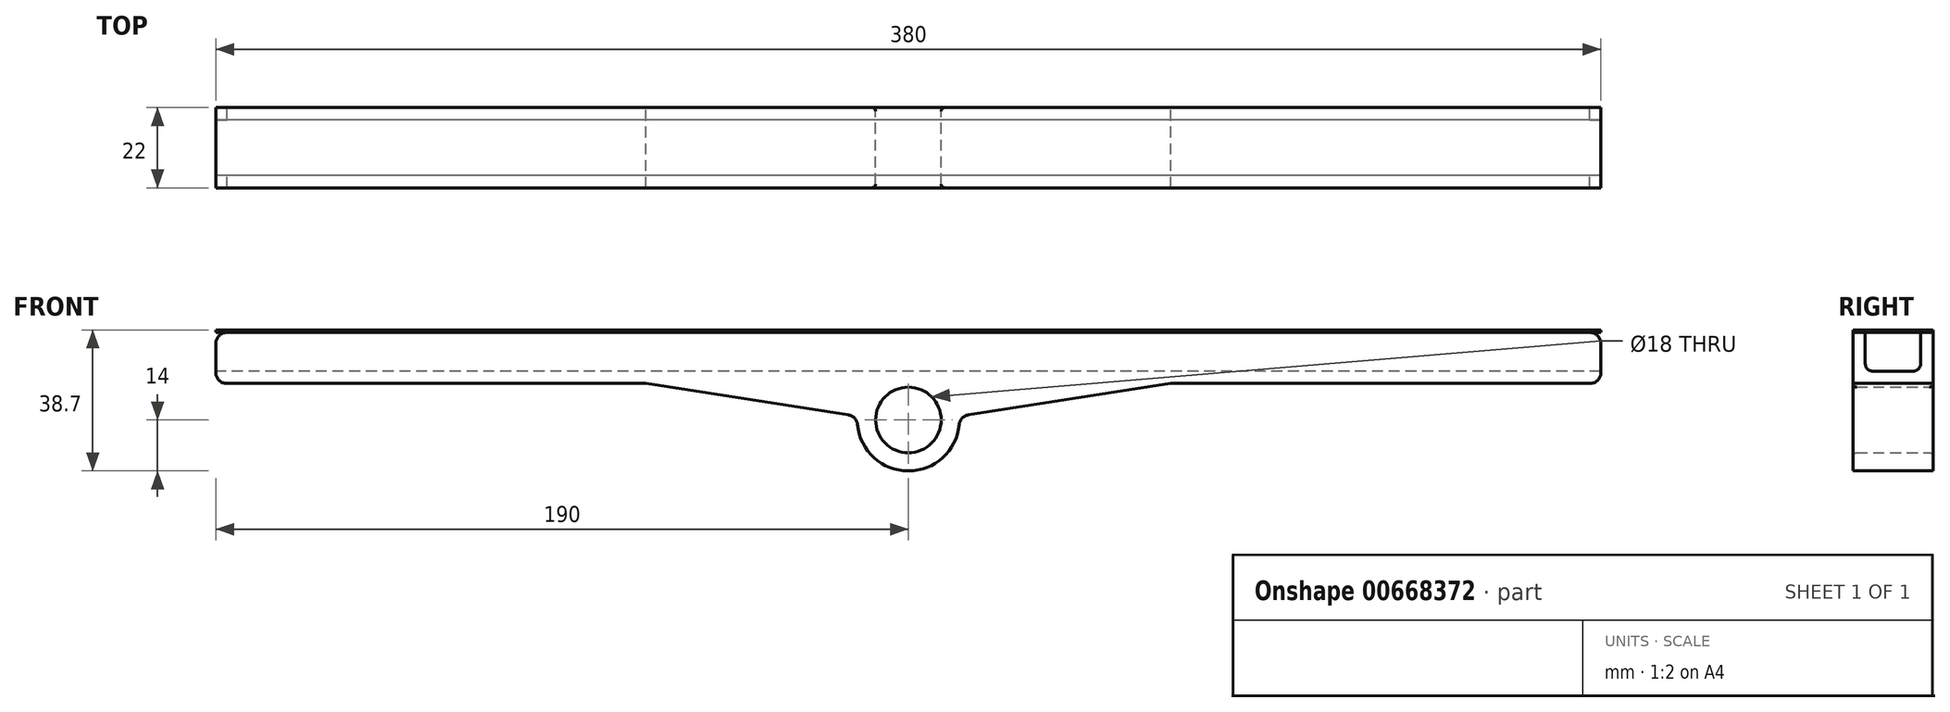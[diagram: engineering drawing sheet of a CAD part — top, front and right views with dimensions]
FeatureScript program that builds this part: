
annotation { "Feature Type Name" : "Feature", "Feature Type Description" : "" }
export const myFeature = defineFeature(function(context is Context, id is Id, definition is map)
    precondition{}
    {
        {
            assignVariable(context, id + "F0", {"name" : "TrayThickness", "anyValue" : 22});
        }
        {
            var Q0;
            Q0=qCreatedBy(makeId("Front.planeOp"),FACE);
            var sketch = newSketch(context, id + "F1", { "sketchPlane" : qUnion([Q0])});
            skLineSegment(sketch, "E0", {"start": v(-190, 159.54) * mm, "end": v(-190, -158.49) * mm, "construction": true});
            skLineSegment(sketch, "E1", {"start": v(190, 159.54) * mm, "end": v(190, -158.49) * mm, "construction": true});
            skLineSegment(sketch, "E2", {"start": v(-190, 14) * mm, "end": v(190, 14) * mm});
            skLineSegment(sketch, "E3", {"start": v(190, 14) * mm, "end": v(190, 0) * mm});
            skLineSegment(sketch, "E4", {"start": v(190, 0) * mm, "end": v(-190, 0) * mm});
            skLineSegment(sketch, "E5", {"start": v(-190, 0) * mm, "end": v(-190, 14) * mm});
            skSolve(sketch);
        }
        {
            var Q0;
            Q0=makeQuery(id+"F1.imprint","IMPRINT",FACE,{"disambiguationData":[TD([[makeQuery(id+"F1.imprint","IMPRINT",EDGE,{"derivedFrom":sQuery(id+"F1.wireOp",EDGE,"E2")}),-1.0]])]});
            extrude(context, id + "F2", {"entities" : qUnion([Q0]), "endBound" : BoundingType.SYMMETRIC, "depth" : (getVariable(context, 'TrayThickness')) * mm, "offsetDistance" : 25 * mm});
        }
        {
            var Q0;
            Q0=makeQuery(id+"F2.opExtrude","SWEPT_FACE",FACE,{"disambiguationData":[OSD([sQuery(id+"F1.wireOp",EDGE,"E5")])]});
            var sketch = newSketch(context, id + "F3", { "sketchPlane" : qUnion([Q0])});
            skLineSegment(sketch, "E6", {"start": v(-7.6, 14) * mm, "end": v(-7.6, 5.4) * mm});
            skLineSegment(sketch, "E7", {"start": v(-5.6, 3.4) * mm, "end": v(5.6, 3.4) * mm});
            skLineSegment(sketch, "E8", {"start": v(7.6, 5.4) * mm, "end": v(7.6, 14) * mm});
            skPoint(sketch, "E9.visualSharp", {"position": v(-7.6, 3.4) * mm});
            skArc(sketch, "E9.filletArc", {"start": v(-7.6, 5.4) * mm, "mid": v(-7.01, 3.99) * mm, "end": v(-5.6, 3.4) * mm});
            skPoint(sketch, "E10.visualSharp", {"position": v(7.6, 3.4) * mm});
            skArc(sketch, "E10.filletArc", {"start": v(5.6, 3.4) * mm, "mid": v(7.01, 3.99) * mm, "end": v(7.6, 5.4) * mm});
            skSolve(sketch);
        }
        {
            var Q0;
            {var subQ1=sQuery(id+"F3.wireOp",EDGE,"E6");Q0=makeQuery(id+"F3.imprint","IMPRINT",FACE,{"disambiguationData":[TD([[makeQuery(id+"F3.imprint","IMPRINT",EDGE,{"derivedFrom":subQ1}),1.0]])]});}
            extrude(context, id + "F4", {"entities" : qUnion([Q0]), "operationType" : NewBodyOperationType.REMOVE, "endBound" : BoundingType.THROUGH_ALL, "oppositeDirection" : true, "depth" : 25 * mm, "offsetDistance" : 25 * mm});
        }
        {
            var Q0;
            Q0=makeQuery(id+"F2.opExtrude","CAP_FACE",FACE,{"disambiguationData":[OSD([sQuery(id+"F1.wireOp",EDGE,"E2"),sQuery(id+"F1.wireOp",EDGE,"E3"),sQuery(id+"F1.wireOp",EDGE,"E4"),sQuery(id+"F1.wireOp",EDGE,"E5")])],"isStart":true});
            var sketch = newSketch(context, id + "F5", { "sketchPlane" : qUnion([Q0])});
            skLineSegment(sketch, "E11", {"start": v(-72, 0) * mm, "end": v(-13.96, -9) * mm});
            skCircle(sketch, "E12", {"center": v(0, -10) * mm, "radius": 9 * mm});
            skCircle(sketch, "E13", {"center": v(0, -10) * mm, "radius": 14 * mm});
            skLineSegment(sketch, "E14", {"start": v(13.96, -9) * mm, "end": v(72, 0) * mm});
            skSolve(sketch);
        }
        {
            var Q0;
            {var subQ0=sQuery(id+"F5.wireOp",EDGE,"E11");Q0=makeQuery(id+"F5.imprint","IMPRINT",FACE,{"disambiguationData":[TD([[makeQuery(id+"F5.imprint","IMPRINT",EDGE,{"derivedFrom":subQ0}),1.0]])]});}
            var Q1;
            Q1=makeQuery(id+"F5.imprint","IMPRINT",FACE,{"disambiguationData":[TD([[makeQuery(id+"F5.imprint","IMPRINT",EDGE,{"derivedFrom":sQuery(id+"F5.wireOp",EDGE,"E12")}),-1.0]])]});
            var Q2;
            {var subQ0=sQuery(id+"F5.wireOp",EDGE,"E14");Q2=makeQuery(id+"F5.imprint","IMPRINT",FACE,{"disambiguationData":[TD([[makeQuery(id+"F5.imprint","IMPRINT",EDGE,{"derivedFrom":subQ0}),1.0]])]});}
            var Q3;
            Q3=makeQuery(id+"F2.opExtrude","CAP_FACE",FACE,{"disambiguationData":[OSD([sQuery(id+"F1.wireOp",EDGE,"E2"),sQuery(id+"F1.wireOp",EDGE,"E3"),sQuery(id+"F1.wireOp",EDGE,"E4"),sQuery(id+"F1.wireOp",EDGE,"E5")])],"isStart":false});
            extrude(context, id + "F6", {"entities" : qUnion([Q0, Q1, Q2]), "operationType" : NewBodyOperationType.ADD, "endBound" : BoundingType.UP_TO_SURFACE, "oppositeDirection" : true, "depth" : 25 * mm, "endBoundEntityFace" : qUnion([Q3]), "offsetDistance" : 25 * mm});
        }
        {
            var Q0;
            {var subQ2=sQuery(id+"F1.wireOp",EDGE,"E2");Q0=makeQuery(id+"F4.boolean.opBoolean","SPLIT",FACE,{"disambiguationData":[TD([makeQuery(id+"F4.opExtrude","SWEPT_FACE",FACE,{"disambiguationData":[OSD([sQuery(id+"F3.wireOp",EDGE,"E8")])]})])],"derivedFrom":makeQuery(id+"F2.opExtrude","SWEPT_FACE",FACE,{"disambiguationData":[OSD([subQ2])]})});}
            var sketch = newSketch(context, id + "F7", { "sketchPlane" : qUnion([Q0])});
            skLineSegment(sketch, "E15.bottom", {"start": v(-190, 11) * mm, "end": v(190, 11) * mm});
            skLineSegment(sketch, "E15.top", {"start": v(-190, -11) * mm, "end": v(190, -11) * mm});
            skLineSegment(sketch, "E15.left", {"start": v(-190, 11) * mm, "end": v(-190, -11) * mm});
            skLineSegment(sketch, "E15.right", {"start": v(190, 11) * mm, "end": v(190, -11) * mm});
            skSolve(sketch);
        }
        {
            var Q0;
            {var subQ0=sQuery(id+"F1.wireOp",EDGE,"E2");var subQ1=sQuery(id+"F1.wireOp",EDGE,"E3");Q0=makeQuery(id+"F4.boolean.opBoolean","SPLIT",EDGE,{"disambiguationData":[TD([makeQuery(id+"F4.opExtrude","SWEPT_FACE",FACE,{"disambiguationData":[OSD([sQuery(id+"F3.wireOp",EDGE,"E8")])]})])],"derivedFrom":makeQuery(id+"F2.opExtrude","SWEPT_EDGE",EDGE,{"disambiguationData":[OSD([subQ0,subQ1])]})});}
            var Q1;
            {var subQ0=sQuery(id+"F1.wireOp",EDGE,"E2");var subQ1=sQuery(id+"F1.wireOp",EDGE,"E3");Q1=makeQuery(id+"F4.boolean.opBoolean","SPLIT",EDGE,{"disambiguationData":[TD([makeQuery(id+"F4.opExtrude","SWEPT_FACE",FACE,{"disambiguationData":[OSD([sQuery(id+"F3.wireOp",EDGE,"E6")])]})])],"derivedFrom":makeQuery(id+"F2.opExtrude","SWEPT_EDGE",EDGE,{"disambiguationData":[OSD([subQ0,subQ1])]})});}
            var Q2;
            Q2=makeQuery(id+"F2.opExtrude","SWEPT_EDGE",EDGE,{"disambiguationData":[OSD([sQuery(id+"F1.wireOp",EDGE,"E3"),sQuery(id+"F1.wireOp",EDGE,"E4")])]});
            var Q3;
            {var subQ0=sQuery(id+"F1.wireOp",EDGE,"E2");var subQ1=sQuery(id+"F1.wireOp",EDGE,"E5");Q3=makeQuery(id+"F4.boolean.opBoolean","SPLIT",EDGE,{"disambiguationData":[TD([makeQuery(id+"F4.opExtrude","SWEPT_FACE",FACE,{"disambiguationData":[OSD([sQuery(id+"F3.wireOp",EDGE,"E8")])]})])],"derivedFrom":makeQuery(id+"F2.opExtrude","SWEPT_EDGE",EDGE,{"disambiguationData":[OSD([subQ0,subQ1])]})});}
            var Q4;
            {var subQ0=sQuery(id+"F1.wireOp",EDGE,"E2");var subQ1=sQuery(id+"F1.wireOp",EDGE,"E5");Q4=makeQuery(id+"F4.boolean.opBoolean","SPLIT",EDGE,{"disambiguationData":[TD([makeQuery(id+"F4.opExtrude","SWEPT_FACE",FACE,{"disambiguationData":[OSD([sQuery(id+"F3.wireOp",EDGE,"E6")])]})])],"derivedFrom":makeQuery(id+"F2.opExtrude","SWEPT_EDGE",EDGE,{"disambiguationData":[OSD([subQ0,subQ1])]})});}
            var Q5;
            Q5=makeQuery(id+"F2.opExtrude","SWEPT_EDGE",EDGE,{"disambiguationData":[OSD([sQuery(id+"F1.wireOp",EDGE,"E4"),sQuery(id+"F1.wireOp",EDGE,"E5")])]});
            var Q6;
            Q6=makeQuery(id+"F6.opExtrude","SWEPT_EDGE",EDGE,{"disambiguationData":[OSD([sQuery(id+"F5.wireOp",EDGE,"E11"),sQuery(id+"F5.wireOp",EDGE,"E13")])]});
            var Q7;
            Q7=makeQuery(id+"F6.opExtrude","SWEPT_EDGE",EDGE,{"disambiguationData":[OSD([sQuery(id+"F5.wireOp",EDGE,"E13"),sQuery(id+"F5.wireOp",EDGE,"E14")])]});
            fillet(context, id + "F8", {"entities" : qUnion([Q0, Q1, Q2, Q3, Q4, Q5, Q6, Q7]), "radius" : 3 * mm, "tangentPropagation" : true, "allowEdgeOverflow" : false});
        }
        {
            var Q0;
            Q0 = qSketchRegion(id + "F7", true);
            extrude(context, id + "F9", {"entities" : qUnion([Q0]), "operationType" : NewBodyOperationType.ADD, "depth" : 0.7 * mm, "offsetDistance" : 25 * mm});
        }
        {
            var Q0;
            Q0=makeQuery(id+"F6.opExtrude","SWEPT_FACE",FACE,{"disambiguationData":[OSD([sQuery(id+"F5.wireOp",EDGE,"E12")])]});
            fillet(context, id + "F10", {"entities" : qUnion([Q0]), "radius" : 1 * mm, "tangentPropagation" : true, "allowEdgeOverflow" : false});
        }
    });
